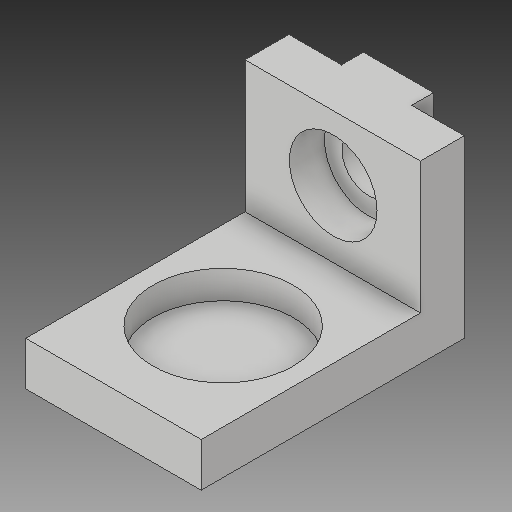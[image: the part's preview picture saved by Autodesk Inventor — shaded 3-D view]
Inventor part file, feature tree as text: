
AUTODESK INVENTOR PART (.ipt)
format: ipt  version: 2019 (Build 230136000, 136)  size: 160,256 bytes
history: native  units: in
note: dims shown in document units (in); Inventor stores cm internally (conversion verified against a paired STEP export)
features: sketch x4, projected_geometry x3, extrude x2, hole x2
ambient origin geometry x8: Origin, YZ Plane, XZ Plane, XY Plane, X Axis, Y Axis, Z Axis, Center Point
bodies: Solid1 (feature_tree)
feature tree (11):
  extrude  "Extrusion1"  Depth=0.5in
  hole  "Hole2"  [1 undecoded]
  extrude  "Extrusion2"  Depth=0.2in
  hole  "Hole3"  [1 undecoded]
  sketch  "Sketch1"  dims[d0=0.125in d1=0.5in]
  sketch  "Sketch3"  dims[d4=0.125in d5=0.75in]
  projected_geometry  "Projected Loop2"
  sketch  "Sketch4"  dims[d6=0.5in d7=0.0in]
  projected_geometry  "Projected Loop3"
  sketch  "Sketch5"  dims[d15=0.4in d16=0.75in d17=0.375in d18=0.25in d19=0.5635in d20=0.08in d21=0.0in d22=0.2in d23=0.5in d24=0.15in d25=0.0625in d26=0.0in d27=0.15in d28=0.75in d29=0.25in d30=0.1in d31=0.5635in d32=1.0in d33=0.8108in]
  projected_geometry  "Projected Loop4"
note: 2 required parameter values undecoded (feature->parameter linkage not recoverable at this tier; creation-order binding heuristic only, values carry confidence <= 0.55)
